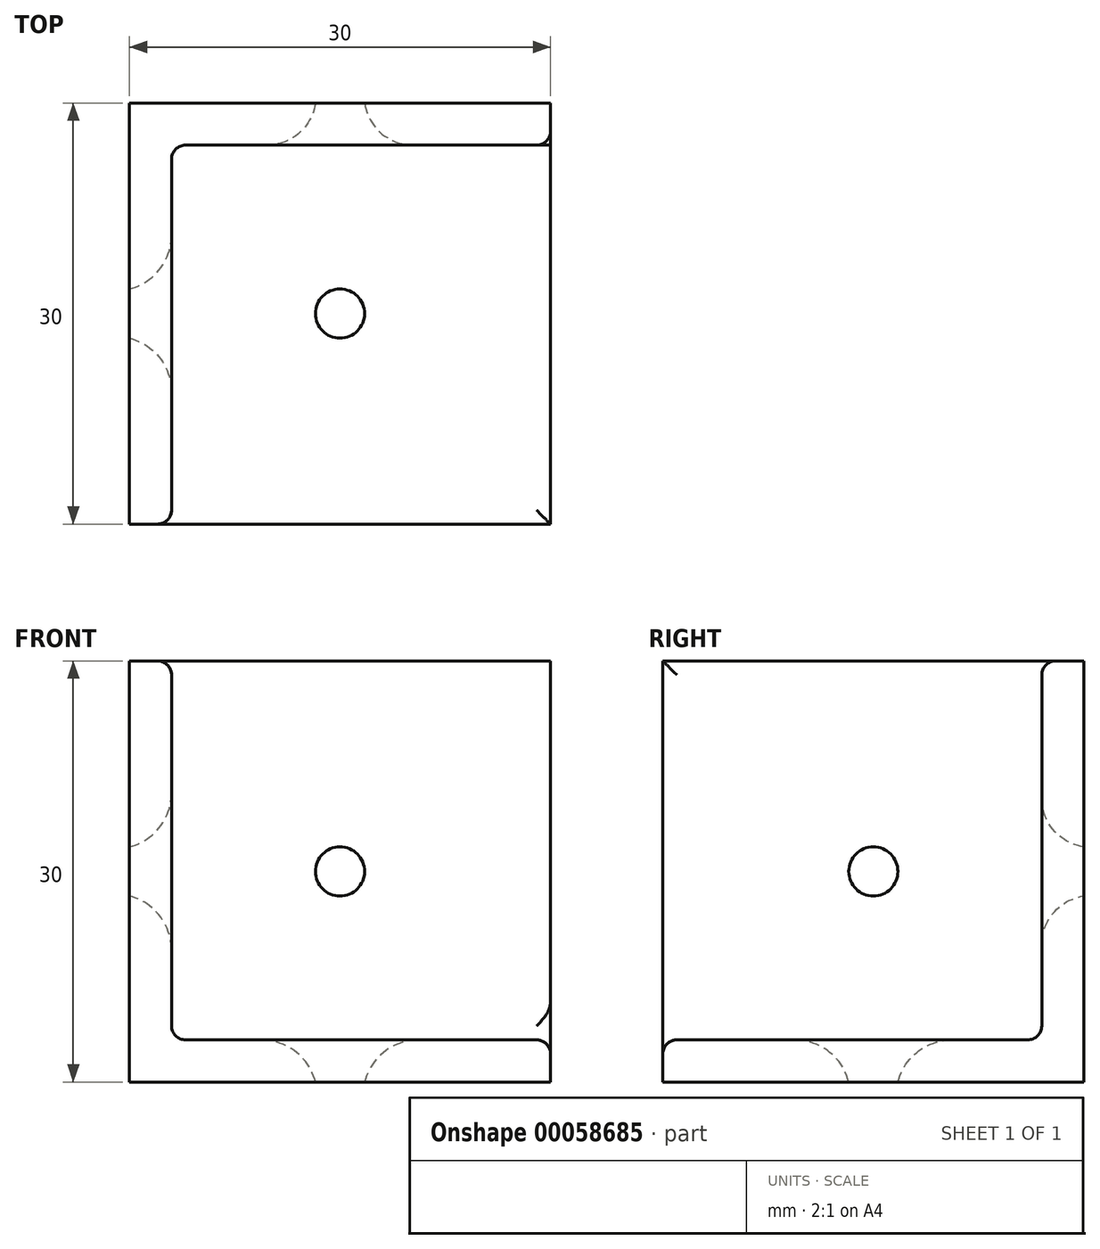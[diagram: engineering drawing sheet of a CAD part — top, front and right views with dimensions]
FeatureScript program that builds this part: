
annotation { "Feature Type Name" : "Feature", "Feature Type Description" : "" }
export const myFeature = defineFeature(function(context is Context, id is Id, definition is map)
    precondition{}
    {
        {
            var Q0;
            Q0=qCreatedBy(makeId("Top.planeOp"),FACE);
            var sketch = newSketch(context, id + "F0", { "sketchPlane" : qUnion([Q0])});
            skLineSegment(sketch, "E0.bottom", {"start": v(0, 0) * mm, "end": v(30, 0) * mm});
            skLineSegment(sketch, "E0.top", {"start": v(0, 30) * mm, "end": v(30, 30) * mm});
            skLineSegment(sketch, "E0.left", {"start": v(0, 0) * mm, "end": v(0, 30) * mm});
            skLineSegment(sketch, "E0.right", {"start": v(30, 0) * mm, "end": v(30, 30) * mm});
            skLineSegment(sketch, "E1", {"start": v(0, 0) * mm, "end": v(30, 30) * mm, "construction": true});
            skLineSegment(sketch, "E2", {"start": v(0, 30) * mm, "end": v(30, 0) * mm, "construction": true});
            skPoint(sketch, "E3", {"position": v(15, 15) * mm});
            skCircle(sketch, "E4", {"center": v(15, 15) * mm, "radius": 1.75 * mm});
            skSolve(sketch);
        }
        {
            var Q0;
            Q0=qCreatedBy(makeId("Right.planeOp"),FACE);
            var sketch = newSketch(context, id + "F1", { "sketchPlane" : qUnion([Q0])});
            skLineSegment(sketch, "E5.bottom", {"start": v(0, 0) * mm, "end": v(30, 0) * mm});
            skLineSegment(sketch, "E5.top", {"start": v(0, 30) * mm, "end": v(30, 30) * mm});
            skLineSegment(sketch, "E5.left", {"start": v(0, 0) * mm, "end": v(0, 30) * mm});
            skLineSegment(sketch, "E5.right", {"start": v(30, 0) * mm, "end": v(30, 30) * mm});
            skLineSegment(sketch, "E6", {"start": v(0, 0) * mm, "end": v(30, 30) * mm, "construction": true});
            skLineSegment(sketch, "E7", {"start": v(0, 30) * mm, "end": v(30, 0) * mm, "construction": true});
            skPoint(sketch, "E8", {"position": v(15, 15) * mm});
            skCircle(sketch, "E9", {"center": v(15, 15) * mm, "radius": 1.75 * mm});
            skSolve(sketch);
        }
        {
            var Q0;
            Q0=makeQuery(id+"F1.imprint","IMPRINT",FACE,{"disambiguationData":[TD([[makeQuery(id+"F1.imprint","IMPRINT",EDGE,{"derivedFrom":sQuery(id+"F1.wireOp",EDGE,"E5.bottom")}),1.0]])]});
            extrude(context, id + "F2", {"entities" : qUnion([Q0]), "depth" : 3 * mm});
        }
        {
            var Q0;
            Q0=makeQuery(id+"F0.imprint","IMPRINT",FACE,{"disambiguationData":[TD([[makeQuery(id+"F0.imprint","IMPRINT",EDGE,{"derivedFrom":sQuery(id+"F0.wireOp",EDGE,"E0.bottom")}),1.0]])]});
            extrude(context, id + "F3", {"entities" : qUnion([Q0]), "operationType" : NewBodyOperationType.ADD, "depth" : 3 * mm});
        }
        {
            var Q0;
            Q0=makeQuery(id+"F3.boolean.opBoolean","MERGE",EDGE,{"derivedFrom":[makeQuery(id+"F2.opExtrude","SWEPT_EDGE",EDGE,{"disambiguationData":[OSD([sQuery(id+"F1.wireOp",EDGE,"E5.bottom"),sQuery(id+"F1.wireOp",EDGE,"E5.right")])]}),makeQuery(id+"F3.opExtrude","CAP_EDGE",EDGE,{"disambiguationData":[OSD([sQuery(id+"F0.wireOp",EDGE,"E0.top")])],"isStart":true})]});
            cPlane(context, id + "F4", {"entities" : qUnion([Q0]), "cplaneType" : CPlaneType.LINE_ANGLE, "offset" : 150 * mm, "angle" : 0 * degree, "width" : 150 * mm, "height" : 150 * mm});
        }
        {
            var Q0;
            Q0=qCreatedBy(id+"F4.planeOp",FACE);
            var sketch = newSketch(context, id + "F5", { "sketchPlane" : qUnion([Q0])});
            skLineSegment(sketch, "E10.bottom", {"start": v(0, 0) * mm, "end": v(30, 0) * mm});
            skLineSegment(sketch, "E10.top", {"start": v(0, 30) * mm, "end": v(30, 30) * mm});
            skLineSegment(sketch, "E10.left", {"start": v(0, 0) * mm, "end": v(0, 30) * mm});
            skLineSegment(sketch, "E10.right", {"start": v(30, 0) * mm, "end": v(30, 30) * mm});
            skLineSegment(sketch, "E11", {"start": v(0, 0) * mm, "end": v(30, 30) * mm, "construction": true});
            skLineSegment(sketch, "E12", {"start": v(0, 30) * mm, "end": v(30, 0) * mm, "construction": true});
            skPoint(sketch, "E13", {"position": v(15, 15) * mm});
            skCircle(sketch, "E14", {"center": v(15, 15) * mm, "radius": 1.75 * mm});
            skSolve(sketch);
        }
        {
            var Q0;
            Q0=makeQuery(id+"F5.imprint","IMPRINT",FACE,{"disambiguationData":[TD([[makeQuery(id+"F5.imprint","IMPRINT",EDGE,{"derivedFrom":sQuery(id+"F5.wireOp",EDGE,"E10.bottom")}),1.0]])]});
            extrude(context, id + "F6", {"entities" : qUnion([Q0]), "operationType" : NewBodyOperationType.ADD, "depth" : 3 * mm});
        }
        {
            var Q0;
            Q0=makeQuery(id+"F3.boolean.opBoolean","INTERSECT",EDGE,{"derivedFrom":[makeQuery(id+"F2.opExtrude","CAP_FACE",FACE,{"disambiguationData":[OSD([sQuery(id+"F1.wireOp",EDGE,"E5.bottom"),sQuery(id+"F1.wireOp",EDGE,"E5.top"),sQuery(id+"F1.wireOp",EDGE,"E5.left"),sQuery(id+"F1.wireOp",EDGE,"E5.right")])],"isStart":false}),makeQuery(id+"F3.opExtrude","CAP_FACE",FACE,{"disambiguationData":[OSD([sQuery(id+"F0.wireOp",EDGE,"E0.bottom"),sQuery(id+"F0.wireOp",EDGE,"E0.top"),sQuery(id+"F0.wireOp",EDGE,"E0.left"),sQuery(id+"F0.wireOp",EDGE,"E0.right")])],"isStart":false})]});
            var Q1;
            Q1=makeQuery(id+"F2.opExtrude","CAP_EDGE",EDGE,{"disambiguationData":[OSD([sQuery(id+"F1.wireOp",EDGE,"E5.top")])],"isStart":false});
            var Q2;
            Q2=makeQuery(id+"F3.opExtrude","CAP_EDGE",EDGE,{"disambiguationData":[OSD([sQuery(id+"F0.wireOp",EDGE,"E0.right")])],"isStart":false});
            var Q3;
            Q3=makeQuery(id+"F2.opExtrude","CAP_EDGE",EDGE,{"disambiguationData":[OSD([sQuery(id+"F1.wireOp",EDGE,"E5.left")])],"isStart":false});
            var Q4;
            Q4=makeQuery(id+"F2.opExtrude","CAP_EDGE",EDGE,{"disambiguationData":[OSD([sQuery(id+"F1.wireOp",EDGE,"E5.right")])],"isStart":false});
            var Q5;
            Q5=makeQuery(id+"F3.opExtrude","CAP_EDGE",EDGE,{"disambiguationData":[OSD([sQuery(id+"F0.wireOp",EDGE,"E0.bottom")])],"isStart":false});
            var Q6;
            Q6=makeQuery(id+"F3.opExtrude","CAP_EDGE",EDGE,{"disambiguationData":[OSD([sQuery(id+"F0.wireOp",EDGE,"E0.top")])],"isStart":false});
            var Q7;
            Q7=makeQuery(id+"F6.boolean.opBoolean","INTERSECT",EDGE,{"derivedFrom":[makeQuery(id+"F3.opExtrude","CAP_FACE",FACE,{"disambiguationData":[OSD([sQuery(id+"F0.wireOp",EDGE,"E0.bottom"),sQuery(id+"F0.wireOp",EDGE,"E0.top"),sQuery(id+"F0.wireOp",EDGE,"E0.left"),sQuery(id+"F0.wireOp",EDGE,"E0.right"),sQuery(id+"F0.wireOp",EDGE,"E4")])],"isStart":false}),makeQuery(id+"F6.opExtrude","CAP_FACE",FACE,{"disambiguationData":[OSD([sQuery(id+"F5.wireOp",EDGE,"E10.bottom"),sQuery(id+"F5.wireOp",EDGE,"E10.top"),sQuery(id+"F5.wireOp",EDGE,"E10.left"),sQuery(id+"F5.wireOp",EDGE,"E10.right"),sQuery(id+"F5.wireOp",EDGE,"E14")])],"isStart":false})]});
            var Q8;
            Q8=makeQuery(id+"F6.opExtrude","CAP_EDGE",EDGE,{"disambiguationData":[OSD([sQuery(id+"F5.wireOp",EDGE,"E10.top")])],"isStart":false});
            var Q9;
            Q9=makeQuery(id+"F6.boolean.opBoolean","INTERSECT",EDGE,{"derivedFrom":[makeQuery(id+"F2.opExtrude","CAP_FACE",FACE,{"disambiguationData":[OSD([sQuery(id+"F1.wireOp",EDGE,"E5.bottom"),sQuery(id+"F1.wireOp",EDGE,"E5.top"),sQuery(id+"F1.wireOp",EDGE,"E5.left"),sQuery(id+"F1.wireOp",EDGE,"E5.right"),sQuery(id+"F1.wireOp",EDGE,"E9")])],"isStart":false}),makeQuery(id+"F6.opExtrude","CAP_FACE",FACE,{"disambiguationData":[OSD([sQuery(id+"F5.wireOp",EDGE,"E10.bottom"),sQuery(id+"F5.wireOp",EDGE,"E10.top"),sQuery(id+"F5.wireOp",EDGE,"E10.left"),sQuery(id+"F5.wireOp",EDGE,"E10.right"),sQuery(id+"F5.wireOp",EDGE,"E14")])],"isStart":false})]});
            fillet(context, id + "F7", {"entities" : qUnion([Q0, Q1, Q2, Q3, Q4, Q5, Q6, Q7, Q8, Q9]), "radius" : 1 * mm, "tangentPropagation" : true, "allowEdgeOverflow" : false});
        }
        {
            var Q0;
            Q0=makeQuery(id+"F3.opExtrude","CAP_EDGE",EDGE,{"disambiguationData":[OSD([sQuery(id+"F0.wireOp",EDGE,"E4")])],"isStart":false});
            fillet(context, id + "F8", {"entities" : qUnion([Q0]), "radius" : 4 * mm, "tangentPropagation" : true, "allowEdgeOverflow" : false});
        }
        {
            var Q0;
            Q0=makeQuery(id+"F2.opExtrude","CAP_EDGE",EDGE,{"disambiguationData":[OSD([sQuery(id+"F1.wireOp",EDGE,"E9")])],"isStart":false});
            fillet(context, id + "F9", {"entities" : qUnion([Q0]), "radius" : 4 * mm, "tangentPropagation" : true, "allowEdgeOverflow" : false});
        }
        {
            var Q0;
            Q0=makeQuery(id+"F6.opExtrude","CAP_EDGE",EDGE,{"disambiguationData":[OSD([sQuery(id+"F5.wireOp",EDGE,"E14")])],"isStart":false});
            fillet(context, id + "F10", {"entities" : qUnion([Q0]), "radius" : 3.5 * mm, "tangentPropagation" : true, "allowEdgeOverflow" : false});
        }
    });
